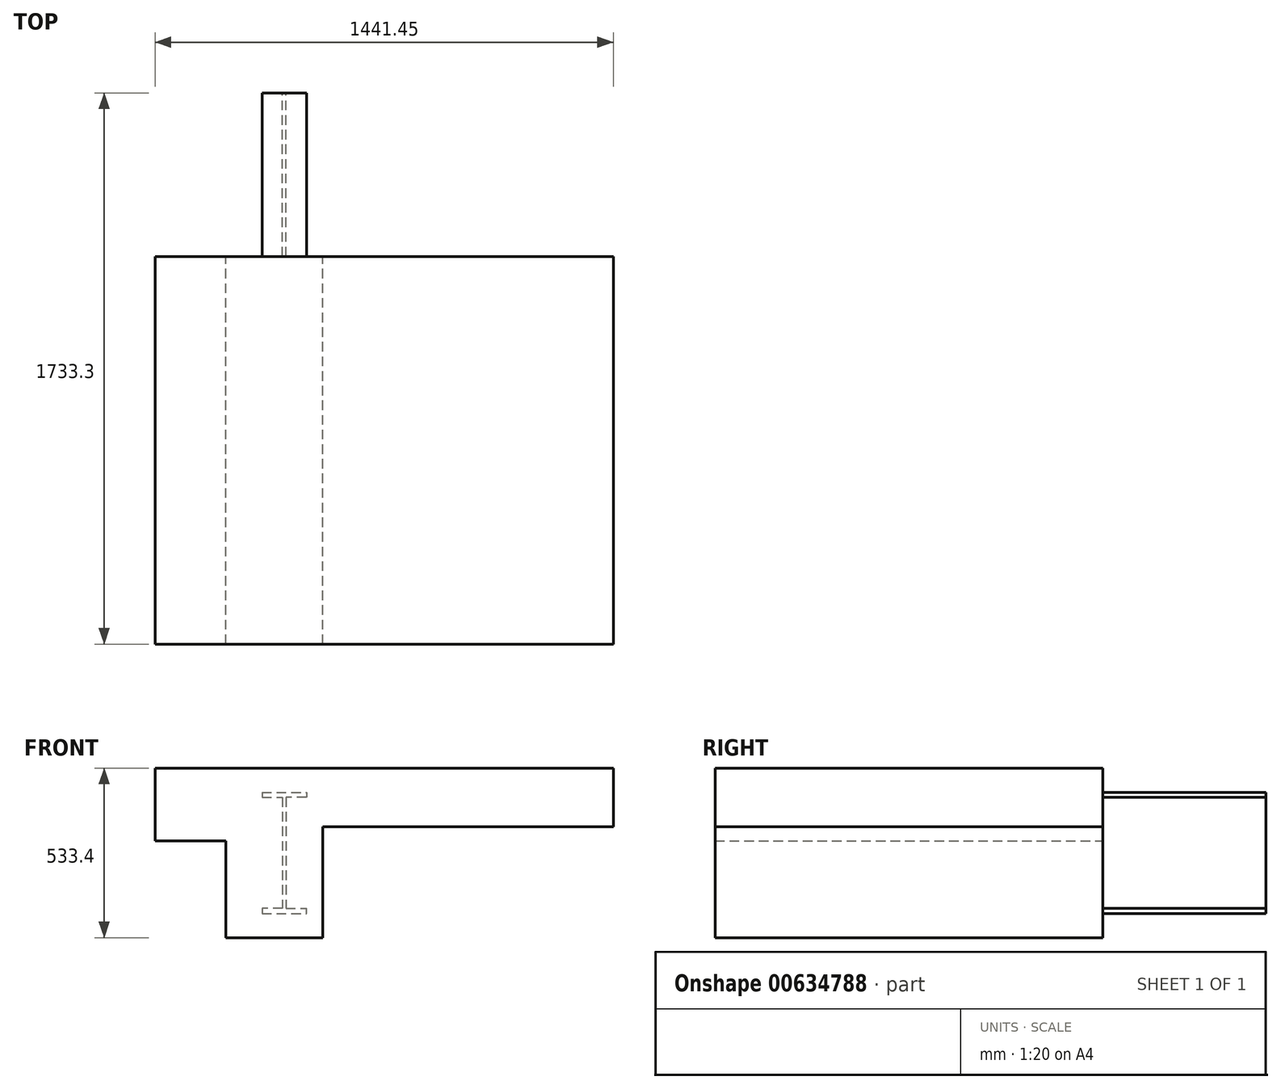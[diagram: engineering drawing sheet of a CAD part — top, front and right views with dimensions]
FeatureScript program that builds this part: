
annotation { "Feature Type Name" : "Feature", "Feature Type Description" : "" }
export const myFeature = defineFeature(function(context is Context, id is Id, definition is map)
    precondition{}
    {
        {
            var Q0;
            Q0=qCreatedBy(makeId("Front.planeOp"),FACE);
            var sketch = newSketch(context, id + "F0", { "sketchPlane" : qUnion([Q0])});
            skLineSegment(sketch, "E0", {"start": v(-69.85, 190.5) * mm, "end": v(69.85, 190.5) * mm});
            skLineSegment(sketch, "E1", {"start": v(69.85, 190.5) * mm, "end": v(69.85, 174.7) * mm});
            skLineSegment(sketch, "E2", {"start": v(69.85, 174.7) * mm, "end": v(5.2, 174.7) * mm});
            skLineSegment(sketch, "E3", {"start": v(5.2, 174.7) * mm, "end": v(5.2, -174.7) * mm});
            skLineSegment(sketch, "E4", {"start": v(5.2, -174.7) * mm, "end": v(69.85, -174.7) * mm});
            skLineSegment(sketch, "E5", {"start": v(-69.85, 190.5) * mm, "end": v(-69.85, 174.7) * mm});
            skLineSegment(sketch, "E6", {"start": v(-69.85, 174.7) * mm, "end": v(-5.2, 174.7) * mm});
            skLineSegment(sketch, "E7", {"start": v(-5.2, 174.7) * mm, "end": v(-5.2, -174.7) * mm});
            skLineSegment(sketch, "E8", {"start": v(-5.2, -174.7) * mm, "end": v(-69.85, -174.7) * mm});
            skLineSegment(sketch, "E9", {"start": v(-69.85, -174.7) * mm, "end": v(-69.85, -190.5) * mm});
            skLineSegment(sketch, "E10", {"start": v(-69.85, -190.5) * mm, "end": v(69.85, -190.5) * mm});
            skLineSegment(sketch, "E11", {"start": v(69.85, -190.5) * mm, "end": v(69.85, -174.7) * mm});
            skLineSegment(sketch, "E12", {"start": v(5.2, 174.7) * mm, "end": v(-5.2, -174.7) * mm, "construction": true});
            skSolve(sketch);
        }
        {
            var Q0;
            Q0 = qSketchRegion(id + "F0", true);
            extrude(context, id + "F1", {"entities" : qUnion([Q0]), "depth" : 514.1 * mm, "offsetDistance" : 25.4 * mm});
        }
        {
            var Q0;
            Q0=makeQuery(id+"F1.opExtrude","CAP_FACE",FACE,{"disambiguationData":[OSD([sQuery(id+"F0.wireOp",EDGE,"E0"),sQuery(id+"F0.wireOp",EDGE,"E1"),sQuery(id+"F0.wireOp",EDGE,"E2"),sQuery(id+"F0.wireOp",EDGE,"E3"),sQuery(id+"F0.wireOp",EDGE,"E4"),sQuery(id+"F0.wireOp",EDGE,"E5"),sQuery(id+"F0.wireOp",EDGE,"E6"),sQuery(id+"F0.wireOp",EDGE,"E7"),sQuery(id+"F0.wireOp",EDGE,"E8"),sQuery(id+"F0.wireOp",EDGE,"E9"),sQuery(id+"F0.wireOp",EDGE,"E10"),sQuery(id+"F0.wireOp",EDGE,"E11")])],"isStart":false});
            var sketch = newSketch(context, id + "F2", { "sketchPlane" : qUnion([Q0])});
            skLineSegment(sketch, "E13", {"start": v(1035.05, 266.7) * mm, "end": v(1035.05, 82.55) * mm});
            skLineSegment(sketch, "E14", {"start": v(1035.05, 82.55) * mm, "end": v(120.65, 82.55) * mm});
            skLineSegment(sketch, "E15", {"start": v(120.65, 82.55) * mm, "end": v(120.65, -266.7) * mm});
            skLineSegment(sketch, "E16", {"start": v(120.65, -266.7) * mm, "end": v(-184.15, -266.7) * mm});
            skLineSegment(sketch, "E17", {"start": v(-184.15, -266.7) * mm, "end": v(-184.15, 38.1) * mm});
            skLineSegment(sketch, "E18", {"start": v(-406.4, 266.7) * mm, "end": v(1035.05, 266.7) * mm});
            skLineSegment(sketch, "E19", {"start": v(-184.15, 38.1) * mm, "end": v(-406.4, 38.1) * mm});
            skLineSegment(sketch, "E20", {"start": v(-406.4, 38.1) * mm, "end": v(-406.4, 266.7) * mm});
            skSolve(sketch);
        }
        {
            var Q0;
            Q0 = qSketchRegion(id + "F2", true);
            extrude(context, id + "F3", {"entities" : qUnion([Q0]), "operationType" : NewBodyOperationType.ADD, "depth" : 1219.2 * mm, "offsetDistance" : 25.4 * mm});
        }
    });
